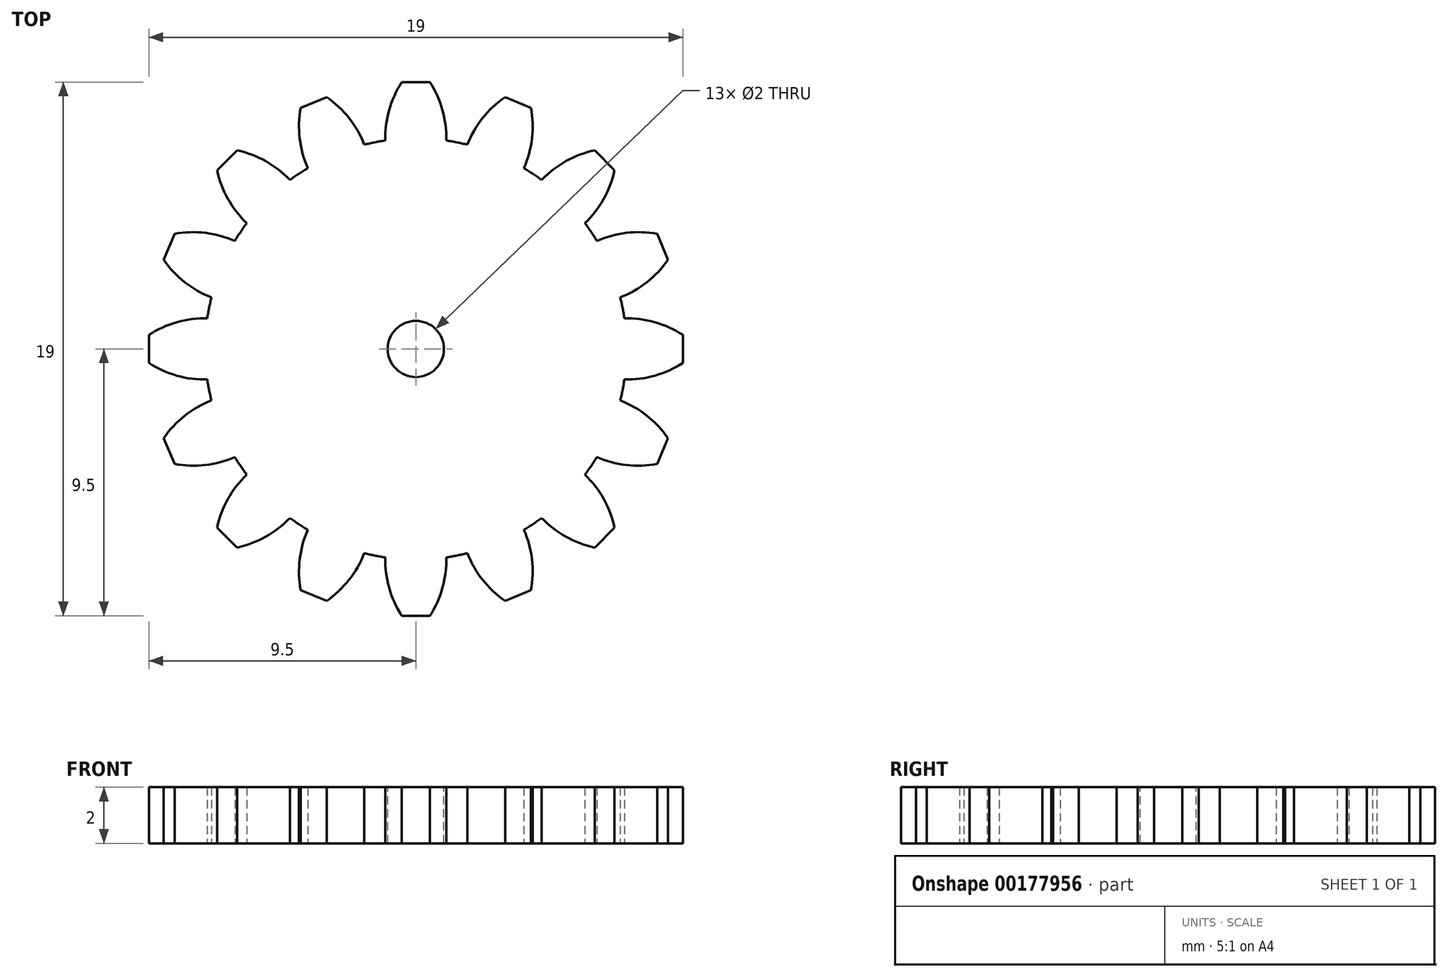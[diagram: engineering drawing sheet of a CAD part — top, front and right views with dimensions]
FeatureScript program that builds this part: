
annotation { "Feature Type Name" : "Feature", "Feature Type Description" : "" }
export const myFeature = defineFeature(function(context is Context, id is Id, definition is map)
    precondition{}
    {
        {
            var Q0;
            Q0=qCreatedBy(makeId("Top.planeOp"),FACE);
            var sketch = newSketch(context, id + "F0", { "sketchPlane" : qUnion([Q0])});
            skCircle(sketch, "E0", {"center": v(0, 0) * mm, "radius": 7.5 * mm});
            skLineSegment(sketch, "E1", {"start": v(0, 0) * mm, "end": v(0, 7.5) * mm, "construction": true});
            skLineSegment(sketch, "E2", {"start": v(0, 7.5) * mm, "end": v(0, 9.5) * mm});
            skLineSegment(sketch, "E3", {"start": v(0, 9.5) * mm, "end": v(-0.5, 9.5) * mm});
            skArc(sketch, "E4", {"start": v(-0.5, 9.5) * mm, "mid": v(-0.95, 8.5) * mm, "end": v(-1.09, 7.42) * mm});
            skLineSegment(sketch, "E5.MirrorCS", {"start": v(0, 9.5) * mm, "end": v(0.5, 9.5) * mm});
            skArc(sketch, "E6.MirrorCS", {"start": v(0.5, 9.5) * mm, "mid": v(0.95, 8.5) * mm, "end": v(1.09, 7.42) * mm});
            skArc(sketch, "E7.1.0", {"start": v(-4.1, 8.59) * mm, "mid": v(-4.13, 7.5) * mm, "end": v(-3.85, 6.44) * mm});
            skLineSegment(sketch, "E7.1.1", {"start": v(-3.64, 8.78) * mm, "end": v(-4.1, 8.59) * mm});
            skLineSegment(sketch, "E7.1.2", {"start": v(-3.64, 8.78) * mm, "end": v(-3.17, 8.97) * mm});
            skArc(sketch, "E7.1.3", {"start": v(-3.17, 8.97) * mm, "mid": v(-2.38, 8.22) * mm, "end": v(-1.83, 7.27) * mm});
            skArc(sketch, "E7.2.0", {"start": v(-7.07, 6.36) * mm, "mid": v(-6.69, 5.34) * mm, "end": v(-6.02, 4.48) * mm});
            skLineSegment(sketch, "E7.2.1", {"start": v(-6.72, 6.72) * mm, "end": v(-7.07, 6.36) * mm});
            skLineSegment(sketch, "E7.2.2", {"start": v(-6.72, 6.72) * mm, "end": v(-6.36, 7.07) * mm});
            skArc(sketch, "E7.2.3", {"start": v(-6.36, 7.07) * mm, "mid": v(-5.34, 6.69) * mm, "end": v(-4.48, 6.02) * mm});
            skArc(sketch, "E7.3.0", {"start": v(-8.97, 3.17) * mm, "mid": v(-8.22, 2.38) * mm, "end": v(-7.27, 1.83) * mm});
            skLineSegment(sketch, "E7.3.1", {"start": v(-8.78, 3.64) * mm, "end": v(-8.97, 3.17) * mm});
            skLineSegment(sketch, "E7.3.2", {"start": v(-8.78, 3.64) * mm, "end": v(-8.59, 4.1) * mm});
            skArc(sketch, "E7.3.3", {"start": v(-8.59, 4.1) * mm, "mid": v(-7.5, 4.13) * mm, "end": v(-6.44, 3.85) * mm});
            skArc(sketch, "E7.4.0", {"start": v(-9.5, -0.5) * mm, "mid": v(-8.5, -0.95) * mm, "end": v(-7.42, -1.09) * mm});
            skLineSegment(sketch, "E7.4.1", {"start": v(-9.5, 0) * mm, "end": v(-9.5, -0.5) * mm});
            skLineSegment(sketch, "E7.4.2", {"start": v(-9.5, 0) * mm, "end": v(-9.5, 0.5) * mm});
            skArc(sketch, "E7.4.3", {"start": v(-9.5, 0.5) * mm, "mid": v(-8.5, 0.95) * mm, "end": v(-7.42, 1.09) * mm});
            skArc(sketch, "E7.5.0", {"start": v(-8.59, -4.1) * mm, "mid": v(-7.5, -4.13) * mm, "end": v(-6.44, -3.85) * mm});
            skLineSegment(sketch, "E7.5.1", {"start": v(-8.78, -3.64) * mm, "end": v(-8.59, -4.1) * mm});
            skLineSegment(sketch, "E7.5.2", {"start": v(-8.78, -3.64) * mm, "end": v(-8.97, -3.17) * mm});
            skArc(sketch, "E7.5.3", {"start": v(-8.97, -3.17) * mm, "mid": v(-8.22, -2.38) * mm, "end": v(-7.27, -1.83) * mm});
            skArc(sketch, "E7.6.0", {"start": v(-6.36, -7.07) * mm, "mid": v(-5.34, -6.69) * mm, "end": v(-4.48, -6.02) * mm});
            skLineSegment(sketch, "E7.6.1", {"start": v(-6.72, -6.72) * mm, "end": v(-6.36, -7.07) * mm});
            skLineSegment(sketch, "E7.6.2", {"start": v(-6.72, -6.72) * mm, "end": v(-7.07, -6.36) * mm});
            skArc(sketch, "E7.6.3", {"start": v(-7.07, -6.36) * mm, "mid": v(-6.69, -5.34) * mm, "end": v(-6.02, -4.48) * mm});
            skArc(sketch, "E7.7.0", {"start": v(-3.17, -8.97) * mm, "mid": v(-2.38, -8.22) * mm, "end": v(-1.83, -7.27) * mm});
            skLineSegment(sketch, "E7.7.1", {"start": v(-3.64, -8.78) * mm, "end": v(-3.17, -8.97) * mm});
            skLineSegment(sketch, "E7.7.2", {"start": v(-3.64, -8.78) * mm, "end": v(-4.1, -8.59) * mm});
            skArc(sketch, "E7.7.3", {"start": v(-4.1, -8.59) * mm, "mid": v(-4.13, -7.5) * mm, "end": v(-3.85, -6.44) * mm});
            skArc(sketch, "E7.8.0", {"start": v(0.5, -9.5) * mm, "mid": v(0.95, -8.5) * mm, "end": v(1.09, -7.42) * mm});
            skLineSegment(sketch, "E7.8.1", {"start": v(0, -9.5) * mm, "end": v(0.5, -9.5) * mm});
            skLineSegment(sketch, "E7.8.2", {"start": v(0, -9.5) * mm, "end": v(-0.5, -9.5) * mm});
            skArc(sketch, "E7.8.3", {"start": v(-0.5, -9.5) * mm, "mid": v(-0.95, -8.5) * mm, "end": v(-1.09, -7.42) * mm});
            skArc(sketch, "E7.9.0", {"start": v(4.1, -8.59) * mm, "mid": v(4.13, -7.5) * mm, "end": v(3.85, -6.44) * mm});
            skLineSegment(sketch, "E7.9.1", {"start": v(3.64, -8.78) * mm, "end": v(4.1, -8.59) * mm});
            skLineSegment(sketch, "E7.9.2", {"start": v(3.64, -8.78) * mm, "end": v(3.17, -8.97) * mm});
            skArc(sketch, "E7.9.3", {"start": v(3.17, -8.97) * mm, "mid": v(2.38, -8.22) * mm, "end": v(1.83, -7.27) * mm});
            skArc(sketch, "E7.10.0", {"start": v(7.07, -6.36) * mm, "mid": v(6.69, -5.34) * mm, "end": v(6.02, -4.48) * mm});
            skLineSegment(sketch, "E7.10.1", {"start": v(6.72, -6.72) * mm, "end": v(7.07, -6.36) * mm});
            skLineSegment(sketch, "E7.10.2", {"start": v(6.72, -6.72) * mm, "end": v(6.36, -7.07) * mm});
            skArc(sketch, "E7.10.3", {"start": v(6.36, -7.07) * mm, "mid": v(5.34, -6.69) * mm, "end": v(4.48, -6.02) * mm});
            skArc(sketch, "E7.11.0", {"start": v(8.97, -3.17) * mm, "mid": v(8.22, -2.38) * mm, "end": v(7.27, -1.83) * mm});
            skLineSegment(sketch, "E7.11.1", {"start": v(8.78, -3.64) * mm, "end": v(8.97, -3.17) * mm});
            skLineSegment(sketch, "E7.11.2", {"start": v(8.78, -3.64) * mm, "end": v(8.59, -4.1) * mm});
            skArc(sketch, "E7.11.3", {"start": v(8.59, -4.1) * mm, "mid": v(7.5, -4.13) * mm, "end": v(6.44, -3.85) * mm});
            skArc(sketch, "E7.12.0", {"start": v(9.5, 0.5) * mm, "mid": v(8.5, 0.95) * mm, "end": v(7.42, 1.09) * mm});
            skLineSegment(sketch, "E7.12.1", {"start": v(9.5, 0) * mm, "end": v(9.5, 0.5) * mm});
            skLineSegment(sketch, "E7.12.2", {"start": v(9.5, 0) * mm, "end": v(9.5, -0.5) * mm});
            skArc(sketch, "E7.12.3", {"start": v(9.5, -0.5) * mm, "mid": v(8.5, -0.95) * mm, "end": v(7.42, -1.09) * mm});
            skArc(sketch, "E7.13.0", {"start": v(8.59, 4.1) * mm, "mid": v(7.5, 4.13) * mm, "end": v(6.44, 3.85) * mm});
            skLineSegment(sketch, "E7.13.1", {"start": v(8.78, 3.64) * mm, "end": v(8.59, 4.1) * mm});
            skLineSegment(sketch, "E7.13.2", {"start": v(8.78, 3.64) * mm, "end": v(8.97, 3.17) * mm});
            skArc(sketch, "E7.13.3", {"start": v(8.97, 3.17) * mm, "mid": v(8.22, 2.38) * mm, "end": v(7.27, 1.83) * mm});
            skArc(sketch, "E7.14.0", {"start": v(6.36, 7.07) * mm, "mid": v(5.34, 6.69) * mm, "end": v(4.48, 6.02) * mm});
            skLineSegment(sketch, "E7.14.1", {"start": v(6.72, 6.72) * mm, "end": v(6.36, 7.07) * mm});
            skLineSegment(sketch, "E7.14.2", {"start": v(6.72, 6.72) * mm, "end": v(7.07, 6.36) * mm});
            skArc(sketch, "E7.14.3", {"start": v(7.07, 6.36) * mm, "mid": v(6.69, 5.34) * mm, "end": v(6.02, 4.48) * mm});
            skArc(sketch, "E7.15.0", {"start": v(3.17, 8.97) * mm, "mid": v(2.38, 8.22) * mm, "end": v(1.83, 7.27) * mm});
            skLineSegment(sketch, "E7.15.1", {"start": v(3.64, 8.78) * mm, "end": v(3.17, 8.97) * mm});
            skLineSegment(sketch, "E7.15.2", {"start": v(3.64, 8.78) * mm, "end": v(4.1, 8.59) * mm});
            skArc(sketch, "E7.15.3", {"start": v(4.1, 8.59) * mm, "mid": v(4.13, 7.5) * mm, "end": v(3.85, 6.44) * mm});
            skSolve(sketch);
        }
        {
            var Q0;
            Q0 = qSketchRegion(id + "F0", true);
            extrude(context, id + "F1", {"entities" : qUnion([Q0]), "depth" : 2 * mm});
        }
        {
            var Q0;
            Q0=makeQuery(id+"F1.opExtrude","CAP_FACE",FACE,{"disambiguationData":[OSD([sQuery(id+"F0.wireOp",EDGE,"E0"),sQuery(id+"F0.wireOp",EDGE,"E3"),sQuery(id+"F0.wireOp",EDGE,"E4"),sQuery(id+"F0.wireOp",EDGE,"E5.MirrorCS"),sQuery(id+"F0.wireOp",EDGE,"E6.MirrorCS"),sQuery(id+"F0.wireOp",EDGE,"E7.1.0"),sQuery(id+"F0.wireOp",EDGE,"E7.1.1"),sQuery(id+"F0.wireOp",EDGE,"E7.1.2"),sQuery(id+"F0.wireOp",EDGE,"E7.1.3"),sQuery(id+"F0.wireOp",EDGE,"E7.2.0"),sQuery(id+"F0.wireOp",EDGE,"E7.2.1"),sQuery(id+"F0.wireOp",EDGE,"E7.2.2"),sQuery(id+"F0.wireOp",EDGE,"E7.2.3"),sQuery(id+"F0.wireOp",EDGE,"E7.3.0"),sQuery(id+"F0.wireOp",EDGE,"E7.3.1"),sQuery(id+"F0.wireOp",EDGE,"E7.3.2"),sQuery(id+"F0.wireOp",EDGE,"E7.3.3"),sQuery(id+"F0.wireOp",EDGE,"E7.4.0"),sQuery(id+"F0.wireOp",EDGE,"E7.4.1"),sQuery(id+"F0.wireOp",EDGE,"E7.4.2"),sQuery(id+"F0.wireOp",EDGE,"E7.4.3"),sQuery(id+"F0.wireOp",EDGE,"E7.5.0"),sQuery(id+"F0.wireOp",EDGE,"E7.5.1"),sQuery(id+"F0.wireOp",EDGE,"E7.5.2"),sQuery(id+"F0.wireOp",EDGE,"E7.5.3"),sQuery(id+"F0.wireOp",EDGE,"E7.6.0"),sQuery(id+"F0.wireOp",EDGE,"E7.6.1"),sQuery(id+"F0.wireOp",EDGE,"E7.6.2"),sQuery(id+"F0.wireOp",EDGE,"E7.6.3"),sQuery(id+"F0.wireOp",EDGE,"E7.7.0"),sQuery(id+"F0.wireOp",EDGE,"E7.7.1"),sQuery(id+"F0.wireOp",EDGE,"E7.7.2"),sQuery(id+"F0.wireOp",EDGE,"E7.7.3"),sQuery(id+"F0.wireOp",EDGE,"E7.8.0"),sQuery(id+"F0.wireOp",EDGE,"E7.8.1"),sQuery(id+"F0.wireOp",EDGE,"E7.8.2"),sQuery(id+"F0.wireOp",EDGE,"E7.8.3"),sQuery(id+"F0.wireOp",EDGE,"E7.9.0"),sQuery(id+"F0.wireOp",EDGE,"E7.9.1"),sQuery(id+"F0.wireOp",EDGE,"E7.9.2"),sQuery(id+"F0.wireOp",EDGE,"E7.9.3"),sQuery(id+"F0.wireOp",EDGE,"E7.10.0"),sQuery(id+"F0.wireOp",EDGE,"E7.10.1"),sQuery(id+"F0.wireOp",EDGE,"E7.10.2"),sQuery(id+"F0.wireOp",EDGE,"E7.10.3"),sQuery(id+"F0.wireOp",EDGE,"E7.11.0"),sQuery(id+"F0.wireOp",EDGE,"E7.11.1"),sQuery(id+"F0.wireOp",EDGE,"E7.11.2"),sQuery(id+"F0.wireOp",EDGE,"E7.11.3"),sQuery(id+"F0.wireOp",EDGE,"E7.12.0"),sQuery(id+"F0.wireOp",EDGE,"E7.12.1"),sQuery(id+"F0.wireOp",EDGE,"E7.12.2"),sQuery(id+"F0.wireOp",EDGE,"E7.12.3"),sQuery(id+"F0.wireOp",EDGE,"E7.13.0"),sQuery(id+"F0.wireOp",EDGE,"E7.13.1"),sQuery(id+"F0.wireOp",EDGE,"E7.13.2"),sQuery(id+"F0.wireOp",EDGE,"E7.13.3"),sQuery(id+"F0.wireOp",EDGE,"E7.14.0"),sQuery(id+"F0.wireOp",EDGE,"E7.14.1"),sQuery(id+"F0.wireOp",EDGE,"E7.14.2"),sQuery(id+"F0.wireOp",EDGE,"E7.14.3"),sQuery(id+"F0.wireOp",EDGE,"E7.15.0"),sQuery(id+"F0.wireOp",EDGE,"E7.15.1"),sQuery(id+"F0.wireOp",EDGE,"E7.15.2"),sQuery(id+"F0.wireOp",EDGE,"E7.15.3")])],"isStart":false});
            var sketch = newSketch(context, id + "F2", { "sketchPlane" : qUnion([Q0])});
            skCircle(sketch, "E8", {"center": v(0, 0) * mm, "radius": 1 * mm});
            skSolve(sketch);
        }
        {
            var Q0;
            Q0 = qSketchRegion(id + "F2", true);
            extrude(context, id + "F3", {"entities" : qUnion([Q0]), "operationType" : NewBodyOperationType.REMOVE, "endBound" : BoundingType.THROUGH_ALL, "oppositeDirection" : true, "depth" : 25 * mm});
        }
    });
